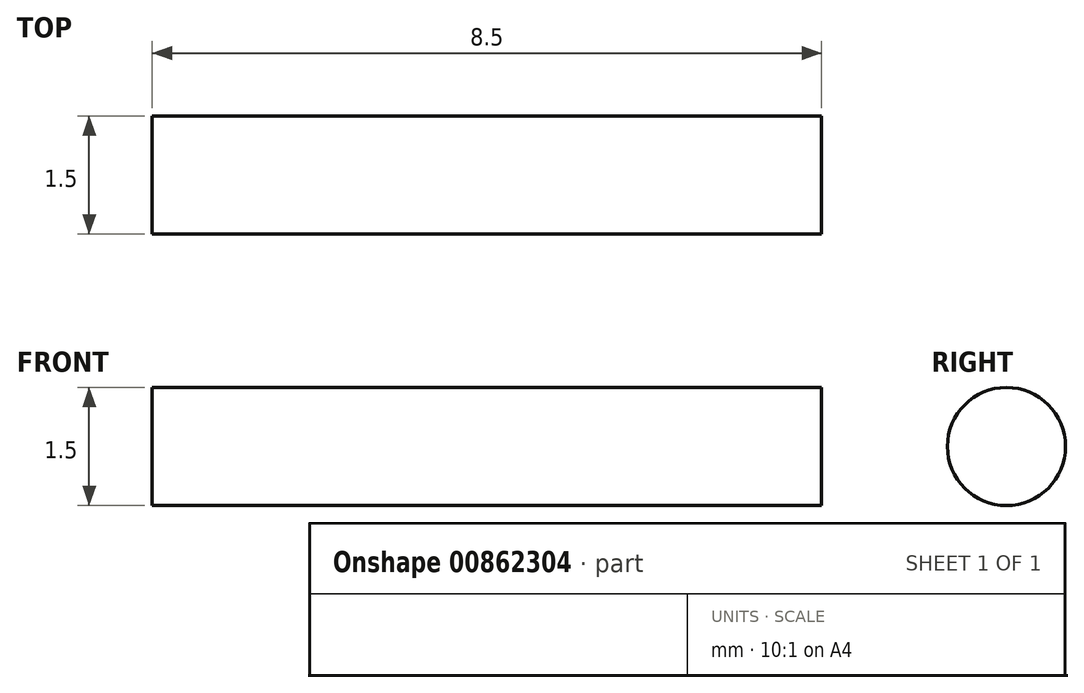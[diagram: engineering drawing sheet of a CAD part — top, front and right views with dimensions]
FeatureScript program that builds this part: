
annotation { "Feature Type Name" : "Feature", "Feature Type Description" : "" }
export const myFeature = defineFeature(function(context is Context, id is Id, definition is map)
    precondition{}
    {
        {
            var Q0;
            Q0=qCreatedBy(makeId("Right.planeOp"),FACE);
            var sketch = newSketch(context, id + "F0", { "sketchPlane" : qUnion([Q0])});
            skCircle(sketch, "E0", {"center": v(0, 0) * mm, "radius": 0.75 * mm});
            skSolve(sketch);
        }
        {
            var Q0;
            Q0 = qSketchRegion(id + "F0", true);
            extrude(context, id + "F1", {"entities" : qUnion([Q0]), "depth" : 8.5 * mm, "offsetDistance" : 25 * mm});
        }
    });
